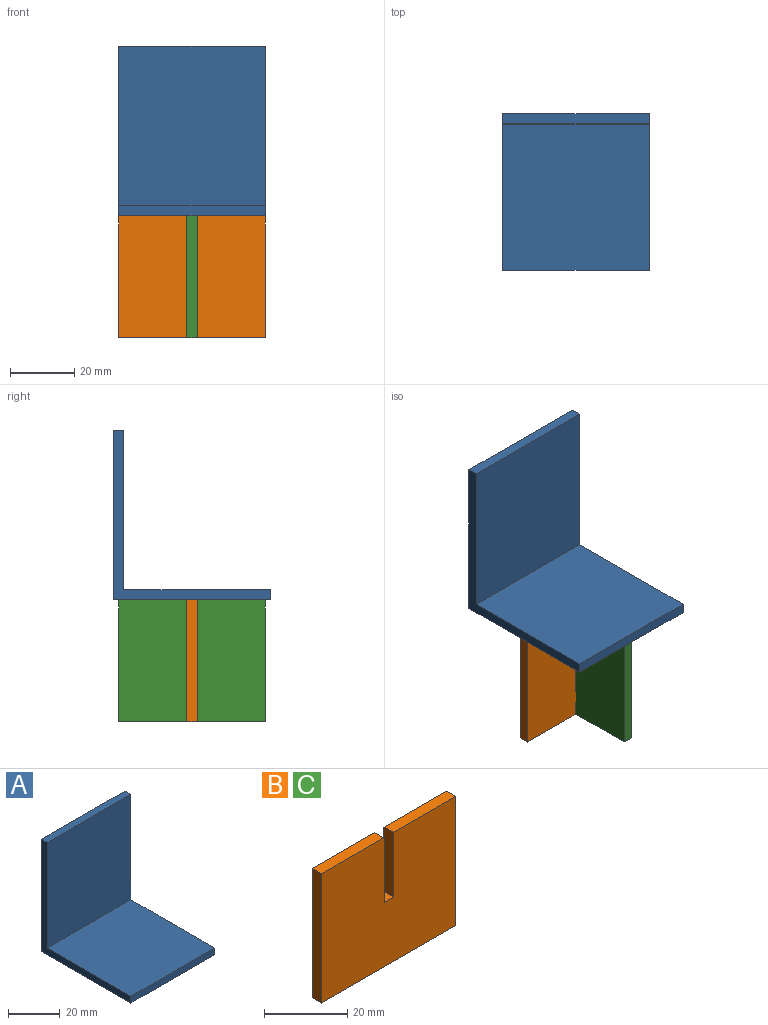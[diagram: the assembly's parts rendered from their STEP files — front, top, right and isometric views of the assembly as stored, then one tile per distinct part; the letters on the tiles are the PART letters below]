
ASSEMBLY  parts=3 mates=2
PART A: 8 faces, bbox 45.7x48.9x53.1 mm
  f0: plane 53.06x48.9mm, normal (-1,0,0), area 313.6mm2, adj f2,f3,f4,f5,f6,f7
  f1: plane 53.06x48.9mm, normal (1,0,0), area 313.6mm2, adj f2,f3,f4,f5,f6,f7
  f2: plane 49.89x45.72mm, normal (0,-1,0), area 2280.8mm2, adj f0,f1,f5,f7
  f3: plane 48.9x45.72mm, normal (0,0,-1), area 2235.5mm2, adj f0,f1,f4,f6
  f4: plane 53.06x45.72mm, normal (0,1,0), area 2426mm2, adj f0,f1,f3,f7
  f5: plane 45.72x45.72mm, normal (0,0,1), area 2090.3mm2, adj f0,f1,f2,f6
  f6: plane 45.72x3.18mm, normal (0,-1,0), area 145.2mm2, adj f0,f1,f3,f5
  f7: plane 45.72x3.18mm, normal (0,0,1), area 145.2mm2, adj f0,f1,f2,f4
PART B: 10 faces, bbox 45.7x3.2x38.1 mm
  f0: plane 45.72x38.1mm, normal (0,-1,0), area 1681.4mm2, adj f1,f2,f4,f5,f6,f7,f8,f9
  f1: plane 38.1x3.18mm, normal (-1,0,0), area 121mm2, adj f0,f3,f8,f9
  f2: plane 38.1x3.18mm, normal (1,0,0), area 121mm2, adj f0,f3,f7,f9
  f3: plane 45.72x38.1mm, normal (0,1,0), area 1681.4mm2, adj f1,f2,f4,f5,f6,f7,f8,f9
  f4: plane 19.05x3.18mm, normal (-1,0,0), area 60.5mm2, adj f0,f3,f6,f7
  f5: plane 19.05x3.18mm, normal (1,0,0), area 60.5mm2, adj f0,f3,f6,f8
  f6: plane 3.18x3.18mm, normal (0,0,1), area 10.1mm2, adj f0,f3,f4,f5
  f7: plane 21.27x3.18mm, normal (0,0,1), area 67.5mm2, adj f0,f2,f3,f4
  f8: plane 21.27x3.18mm, normal (0,0,1), area 67.5mm2, adj f0,f1,f3,f5
  f9: plane 45.72x3.18mm, normal (0,0,-1), area 145.2mm2, adj f0,f1,f2,f3
PART C: same geometry as B
PLACE A t=(71.82,32.03,49.42)mm
PLACE B rot(axis=(1,0,0),180deg) t=(60.81,6,59.27)mm
PLACE C rot(axis=(0,0,-1),90deg) t=(58.5,3.68,1.47)mm
MATE fastened C.f6 <-> B.f6  axis (0,0,1) through (56.91,7.58,30.37)mm
MATE fastened B.f9 <-> A.f3  axis (0,0,1) through (56.91,7.58,49.42)mm
